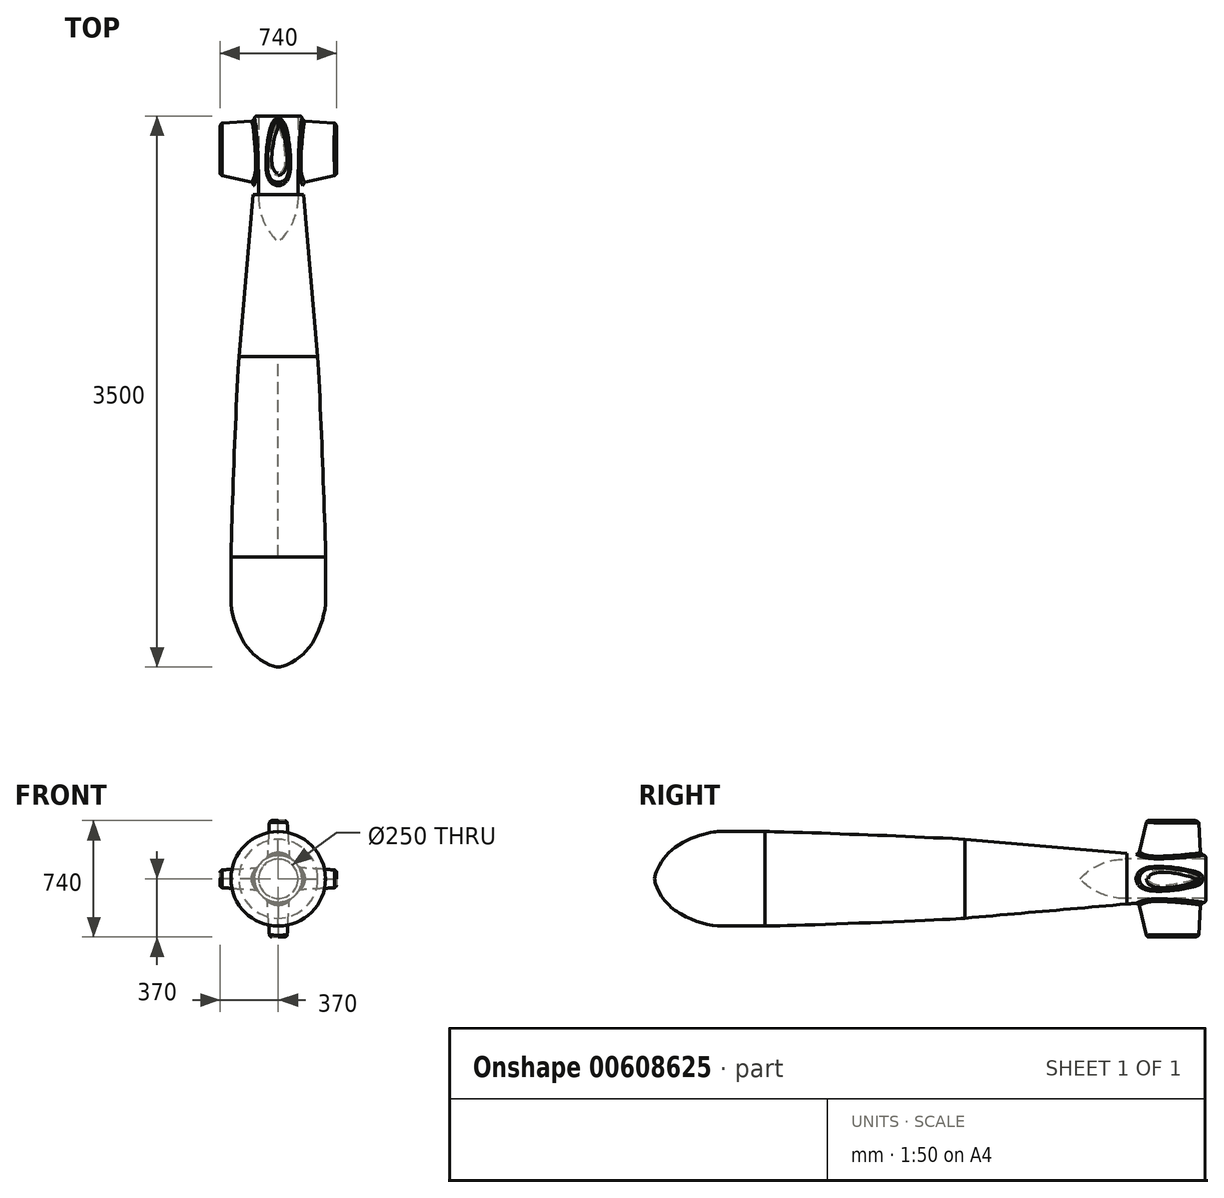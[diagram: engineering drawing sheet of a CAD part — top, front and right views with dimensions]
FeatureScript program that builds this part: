
annotation { "Feature Type Name" : "Feature", "Feature Type Description" : "" }
export const myFeature = defineFeature(function(context is Context, id is Id, definition is map)
    precondition{}
    {
        {
            var Q0;
            Q0=qCreatedBy(makeId("Right.planeOp"),FACE);
            var sketch = newSketch(context, id + "F0", { "sketchPlane" : qUnion([Q0])});
            skLineSegment(sketch, "E0", {"start": v(400, 300) * mm, "end": v(700, 300) * mm});
            skFitSpline(sketch, "E1", {"points": [v(0, 0) * mm, v(130, 200) * mm, v(400, 300) * mm], "startDerivative": vector(31.48, 314.8) * mm, "endDerivative": vector(229.22, 0) * mm});
            skFitSpline(sketch, "E2", {"points": [v(700, 300) * mm, v(1971.3, 250) * mm], "startDerivative": vector(450, 0) * mm, "endDerivative": vector(448.29, -39.22) * mm});
            skLineSegment(sketch, "E3", {"start": v(1971.3, 250) * mm, "end": v(3000, 160) * mm});
            skFitSpline(sketch, "E4", {"points": [v(3000, 160) * mm, v(3160, 150) * mm], "startDerivative": vector(150, -13.12) * mm, "endDerivative": vector(150, 0) * mm});
            skLineSegment(sketch, "E5", {"start": v(3160, 150) * mm, "end": v(3488, 150) * mm});
            skLineSegment(sketch, "E6", {"start": v(3500, 138) * mm, "end": v(3500, 137) * mm});
            skLineSegment(sketch, "E7", {"start": v(3488, 125) * mm, "end": v(2988, 125) * mm});
            skPoint(sketch, "E8.visualSharp", {"position": v(3500, 150) * mm});
            skArc(sketch, "E8.filletArc", {"start": v(3500, 138) * mm, "mid": v(3496.49, 146.49) * mm, "end": v(3488, 150) * mm});
            skPoint(sketch, "E9.visualSharp", {"position": v(3500, 125) * mm});
            skArc(sketch, "E9.filletArc", {"start": v(3488, 125) * mm, "mid": v(3496.49, 128.51) * mm, "end": v(3500, 137) * mm});
            skLineSegment(sketch, "E10", {"start": v(0, 0) * mm, "end": v(2700, 0) * mm});
            skArc(sketch, "E11", {"start": v(2988, 125) * mm, "mid": v(2831.02, 92.4) * mm, "end": v(2700, 0) * mm});
            skSolve(sketch);
        }
        {
            var Q0;
            Q0 = qSketchRegion(id + "F0", true);
            var Q1;
            Q1=sQuery(id+"F0.wireOp",EDGE,"E10");
            revolve(context, id + "F1", {"entities" : qUnion([Q0]), "axis" : qUnion([Q1]), "revolveType" : RevolveType.FULL});
        }
        {
            var Q0;
            Q0=qCreatedBy(makeId("Top.planeOp"),FACE);
            cPlane(context, id + "F2", {"entities" : qUnion([Q0]), "cplaneType" : CPlaneType.OFFSET, "offset" : 130 * mm, "width" : 150 * mm, "height" : 150 * mm});
        }
        {
            var Q0;
            Q0=qCreatedBy(id+"F2.planeOp",FACE);
            var sketch = newSketch(context, id + "F3", { "sketchPlane" : qUnion([Q0])});
            skLineSegment(sketch, "E12", {"start": v(0, 3070) * mm, "end": v(0, 3470) * mm, "construction": true});
            skLineSegment(sketch, "E13", {"start": v(0, 3120) * mm, "end": v(-60, 3120) * mm, "construction": true});
            skLineSegment(sketch, "E14", {"start": v(0, 3420) * mm, "end": v(-40, 3420) * mm, "construction": true});
            skLineSegment(sketch, "E15", {"start": v(-20, 3460) * mm, "end": v(0, 3460) * mm, "construction": true});
            skFitSpline(sketch, "E16", {"points": [v(0, 3070) * mm, v(-60, 3120) * mm, v(-40, 3420) * mm, v(-20, 3460) * mm, v(0, 3470) * mm], "startDerivative": vector(-255.23, 0) * mm, "endDerivative": vector(190.8, 35.78) * mm});
            skFitSpline(sketch, "E17.MirrorCS", {"points": [v(0, 3070) * mm, v(60, 3120) * mm, v(40, 3420) * mm, v(20, 3460) * mm, v(0, 3470) * mm], "startDerivative": vector(255.23, 0) * mm, "endDerivative": vector(-190.8, 35.78) * mm});
            skSolve(sketch);
        }
        {
            var Q0;
            Q0=qCreatedBy(makeId("Top.planeOp"),FACE);
            cPlane(context, id + "F4", {"entities" : qUnion([Q0]), "cplaneType" : CPlaneType.OFFSET, "offset" : 370 * mm, "width" : 150 * mm, "height" : 150 * mm});
        }
        {
            var Q0;
            Q0=qCreatedBy(id+"F4.planeOp",FACE);
            var sketch = newSketch(context, id + "F5", { "sketchPlane" : qUnion([Q0])});
            skLineSegment(sketch, "E18", {"start": v(0, 3125) * mm, "end": v(0, 3455) * mm, "construction": true});
            skLineSegment(sketch, "E19", {"start": v(0, 3175) * mm, "end": v(-50, 3175) * mm, "construction": true});
            skLineSegment(sketch, "E20", {"start": v(-27.5, 3400) * mm, "end": v(0, 3400) * mm, "construction": true});
            skFitSpline(sketch, "E21", {"points": [v(0, 3125) * mm, v(-50, 3175) * mm, v(-27.5, 3400) * mm, v(0, 3455) * mm], "startDerivative": vector(-223.25, 0) * mm, "endDerivative": vector(119.7, 143.64) * mm});
            skLineSegment(sketch, "E22", {"start": v(0, 3425) * mm, "end": v(-18.26, 3425) * mm, "construction": true});
            skFitSpline(sketch, "E23.MirrorCS", {"points": [v(0, 3125) * mm, v(50, 3175) * mm, v(27.5, 3400) * mm, v(0, 3455) * mm], "startDerivative": vector(223.25, 0) * mm, "endDerivative": vector(-119.7, 143.64) * mm});
            skSolve(sketch);
        }
        {
            var Q0;
            Q0 = qSketchRegion(id + "F3", true);
            var Q1;
            Q1 = qSketchRegion(id + "F5", true);
            loft(context, id + "F6", {"sheetProfilesArray" : [{ "sheetProfileEntities" : qUnion([Q0]) }, { "sheetProfileEntities" : qUnion([Q1]) }]});
        }
        {
            var Q0;
            Q0=makeQuery(id+"F6.opLoft","SWEPT_BODY",BODY,{"disambiguationData":[OSD([makeQuery(id+"F3.imprint","IMPRINT",FACE,{"disambiguationData":[TD([[makeQuery(id+"F3.imprint","IMPRINT",EDGE,{"derivedFrom":sQuery(id+"F3.wireOp",EDGE,"E16")}),-1.0]])]}),makeQuery(id+"F5.imprint","IMPRINT",FACE,{"disambiguationData":[TD([[makeQuery(id+"F5.imprint","IMPRINT",EDGE,{"derivedFrom":sQuery(id+"F5.wireOp",EDGE,"E21")}),-1.0]])]})])]});
            var Q1;
            Q1=sQuery(id+"F0.wireOp",EDGE,"E10");
            circularPattern(context, id + "F7", {"entities" : qUnion([Q0]), "axis" : qUnion([Q1]), "angle" : 360 * degree, "instanceCount" : 4, "equalSpace" : true});
        }
        {
            var Q0;
            Q0=makeQuery(id+"F1.opRevolve","SWEPT_BODY",BODY,{"disambiguationData":[OSD([sQuery(id+"F0.wireOp",EDGE,"E0"),sQuery(id+"F0.wireOp",EDGE,"E1"),sQuery(id+"F0.wireOp",EDGE,"E2"),sQuery(id+"F0.wireOp",EDGE,"E3"),sQuery(id+"F0.wireOp",EDGE,"E4"),sQuery(id+"F0.wireOp",EDGE,"E5"),sQuery(id+"F0.wireOp",EDGE,"E6"),sQuery(id+"F0.wireOp",EDGE,"E7"),sQuery(id+"F0.wireOp",EDGE,"E8.filletArc"),sQuery(id+"F0.wireOp",EDGE,"E9.filletArc"),sQuery(id+"F0.wireOp",EDGE,"E10"),sQuery(id+"F0.wireOp",EDGE,"E11")])]});
            var Q1;
            Q1=makeQuery(id+"F6.opLoft","SWEPT_BODY",BODY,{"disambiguationData":[OSD([makeQuery(id+"F3.imprint","IMPRINT",FACE,{"disambiguationData":[TD([[makeQuery(id+"F3.imprint","IMPRINT",EDGE,{"derivedFrom":sQuery(id+"F3.wireOp",EDGE,"E16")}),-1.0]])]}),makeQuery(id+"F5.imprint","IMPRINT",FACE,{"disambiguationData":[TD([[makeQuery(id+"F5.imprint","IMPRINT",EDGE,{"derivedFrom":sQuery(id+"F5.wireOp",EDGE,"E21")}),-1.0]])]})])]});
            var Q2;
            Q2=makeQuery(id+"F7.opPattern","COPY",BODY,{"derivedFrom":makeQuery(id+"F6.opLoft","SWEPT_BODY",BODY,{"disambiguationData":[OSD([makeQuery(id+"F3.imprint","IMPRINT",FACE,{"disambiguationData":[TD([[makeQuery(id+"F3.imprint","IMPRINT",EDGE,{"derivedFrom":sQuery(id+"F3.wireOp",EDGE,"E16")}),-1.0]])]}),makeQuery(id+"F5.imprint","IMPRINT",FACE,{"disambiguationData":[TD([[makeQuery(id+"F5.imprint","IMPRINT",EDGE,{"derivedFrom":sQuery(id+"F5.wireOp",EDGE,"E21")}),-1.0]])]})])]}),"instanceName":"1"});
            var Q3;
            Q3=makeQuery(id+"F7.opPattern","COPY",BODY,{"derivedFrom":makeQuery(id+"F6.opLoft","SWEPT_BODY",BODY,{"disambiguationData":[OSD([makeQuery(id+"F3.imprint","IMPRINT",FACE,{"disambiguationData":[TD([[makeQuery(id+"F3.imprint","IMPRINT",EDGE,{"derivedFrom":sQuery(id+"F3.wireOp",EDGE,"E16")}),-1.0]])]}),makeQuery(id+"F5.imprint","IMPRINT",FACE,{"disambiguationData":[TD([[makeQuery(id+"F5.imprint","IMPRINT",EDGE,{"derivedFrom":sQuery(id+"F5.wireOp",EDGE,"E21")}),-1.0]])]})])]}),"instanceName":"2"});
            var Q4;
            Q4=makeQuery(id+"F7.opPattern","COPY",BODY,{"derivedFrom":makeQuery(id+"F6.opLoft","SWEPT_BODY",BODY,{"disambiguationData":[OSD([makeQuery(id+"F3.imprint","IMPRINT",FACE,{"disambiguationData":[TD([[makeQuery(id+"F3.imprint","IMPRINT",EDGE,{"derivedFrom":sQuery(id+"F3.wireOp",EDGE,"E16")}),-1.0]])]}),makeQuery(id+"F5.imprint","IMPRINT",FACE,{"disambiguationData":[TD([[makeQuery(id+"F5.imprint","IMPRINT",EDGE,{"derivedFrom":sQuery(id+"F5.wireOp",EDGE,"E21")}),-1.0]])]})])]}),"instanceName":"3"});
            booleanBodies(context, id + "F8", {"operationType" : BooleanOperationType.UNION, "tools" : qUnion([Q0, Q1, Q2, Q3, Q4])});
        }
        {
            var Q0;
            {var subQ0=sQuery(id+"F5.wireOp",EDGE,"E23.MirrorCS");var subQ1=sQuery(id+"F5.wireOp",EDGE,"E21");var subQ2=sQuery(id+"F3.wireOp",EDGE,"E17.MirrorCS");var subQ3=sQuery(id+"F3.wireOp",EDGE,"E16");Q0=makeQuery(id+"F8.opBoolean","INTERSECT",EDGE,{"derivedFrom":[makeQuery(id+"F1.opRevolve","SWEPT_FACE",FACE,{"disambiguationData":[OSD([sQuery(id+"F0.wireOp",EDGE,"E5")])]}),makeQuery(id+"F6.opLoft","SWEPT_FACE",FACE,{"disambiguationData":[OSD([subQ3,subQ2,subQ1,subQ0]),TDD([makeQuery(id+"F3.imprint","INTERSECT",VERTEX,{"disambiguationData":[OD(0.0)],"derivedFrom":[subQ3,subQ2]}),makeQuery(id+"F3.imprint","INTERSECT",VERTEX,{"disambiguationData":[OD(1.0)],"derivedFrom":[subQ3,subQ2]}),makeQuery(id+"F3.imprint","IMPRINT",EDGE,{"derivedFrom":subQ2}),makeQuery(id+"F5.imprint","INTERSECT",VERTEX,{"disambiguationData":[OD(0.0)],"derivedFrom":[subQ1,subQ0]}),makeQuery(id+"F5.imprint","INTERSECT",VERTEX,{"disambiguationData":[OD(1.0)],"derivedFrom":[subQ1,subQ0]}),makeQuery(id+"F5.imprint","IMPRINT",EDGE,{"derivedFrom":subQ0})])]})]});}
            var Q1;
            {var subQ0=sQuery(id+"F5.wireOp",EDGE,"E21");var subQ1=sQuery(id+"F5.wireOp",EDGE,"E23.MirrorCS");var subQ2=sQuery(id+"F3.wireOp",EDGE,"E16");var subQ3=sQuery(id+"F3.wireOp",EDGE,"E17.MirrorCS");Q1=makeQuery(id+"F8.opBoolean","INTERSECT",EDGE,{"derivedFrom":[makeQuery(id+"F1.opRevolve","SWEPT_FACE",FACE,{"disambiguationData":[OSD([sQuery(id+"F0.wireOp",EDGE,"E5")])]}),makeQuery(id+"F7.opPattern","COPY",FACE,{"derivedFrom":makeQuery(id+"F6.opLoft","SWEPT_FACE",FACE,{"disambiguationData":[OSD([subQ2,subQ3,subQ0,subQ1]),TDD([makeQuery(id+"F3.imprint","INTERSECT",VERTEX,{"disambiguationData":[OD(0.0)],"derivedFrom":[subQ2,subQ3]}),makeQuery(id+"F3.imprint","INTERSECT",VERTEX,{"disambiguationData":[OD(1.0)],"derivedFrom":[subQ2,subQ3]}),makeQuery(id+"F3.imprint","IMPRINT",EDGE,{"derivedFrom":subQ2}),makeQuery(id+"F5.imprint","INTERSECT",VERTEX,{"disambiguationData":[OD(0.0)],"derivedFrom":[subQ0,subQ1]}),makeQuery(id+"F5.imprint","INTERSECT",VERTEX,{"disambiguationData":[OD(1.0)],"derivedFrom":[subQ0,subQ1]}),makeQuery(id+"F5.imprint","IMPRINT",EDGE,{"derivedFrom":subQ0})])]}),"instanceName":"1"})]});}
            var Q2;
            {var subQ0=sQuery(id+"F5.wireOp",EDGE,"E21");var subQ1=sQuery(id+"F5.wireOp",EDGE,"E23.MirrorCS");var subQ2=sQuery(id+"F3.wireOp",EDGE,"E16");var subQ3=sQuery(id+"F3.wireOp",EDGE,"E17.MirrorCS");Q2=makeQuery(id+"F8.opBoolean","INTERSECT",EDGE,{"derivedFrom":[makeQuery(id+"F1.opRevolve","SWEPT_FACE",FACE,{"disambiguationData":[OSD([sQuery(id+"F0.wireOp",EDGE,"E5")])]}),makeQuery(id+"F7.opPattern","COPY",FACE,{"derivedFrom":makeQuery(id+"F6.opLoft","SWEPT_FACE",FACE,{"disambiguationData":[OSD([subQ2,subQ3,subQ0,subQ1]),TDD([makeQuery(id+"F3.imprint","INTERSECT",VERTEX,{"disambiguationData":[OD(0.0)],"derivedFrom":[subQ2,subQ3]}),makeQuery(id+"F3.imprint","INTERSECT",VERTEX,{"disambiguationData":[OD(1.0)],"derivedFrom":[subQ2,subQ3]}),makeQuery(id+"F3.imprint","IMPRINT",EDGE,{"derivedFrom":subQ2}),makeQuery(id+"F5.imprint","INTERSECT",VERTEX,{"disambiguationData":[OD(0.0)],"derivedFrom":[subQ0,subQ1]}),makeQuery(id+"F5.imprint","INTERSECT",VERTEX,{"disambiguationData":[OD(1.0)],"derivedFrom":[subQ0,subQ1]}),makeQuery(id+"F5.imprint","IMPRINT",EDGE,{"derivedFrom":subQ0})])]}),"instanceName":"2"})]});}
            var Q3;
            {var subQ0=sQuery(id+"F5.wireOp",EDGE,"E21");var subQ1=sQuery(id+"F5.wireOp",EDGE,"E23.MirrorCS");var subQ2=sQuery(id+"F3.wireOp",EDGE,"E16");var subQ3=sQuery(id+"F3.wireOp",EDGE,"E17.MirrorCS");Q3=makeQuery(id+"F8.opBoolean","INTERSECT",EDGE,{"derivedFrom":[makeQuery(id+"F1.opRevolve","SWEPT_FACE",FACE,{"disambiguationData":[OSD([sQuery(id+"F0.wireOp",EDGE,"E5")])]}),makeQuery(id+"F7.opPattern","COPY",FACE,{"derivedFrom":makeQuery(id+"F6.opLoft","SWEPT_FACE",FACE,{"disambiguationData":[OSD([subQ2,subQ3,subQ0,subQ1]),TDD([makeQuery(id+"F3.imprint","INTERSECT",VERTEX,{"disambiguationData":[OD(0.0)],"derivedFrom":[subQ2,subQ3]}),makeQuery(id+"F3.imprint","INTERSECT",VERTEX,{"disambiguationData":[OD(1.0)],"derivedFrom":[subQ2,subQ3]}),makeQuery(id+"F3.imprint","IMPRINT",EDGE,{"derivedFrom":subQ2}),makeQuery(id+"F5.imprint","INTERSECT",VERTEX,{"disambiguationData":[OD(0.0)],"derivedFrom":[subQ0,subQ1]}),makeQuery(id+"F5.imprint","INTERSECT",VERTEX,{"disambiguationData":[OD(1.0)],"derivedFrom":[subQ0,subQ1]}),makeQuery(id+"F5.imprint","IMPRINT",EDGE,{"derivedFrom":subQ0})])]}),"instanceName":"3"})]});}
            fillet(context, id + "F9", {"entities" : qUnion([Q0, Q1, Q2, Q3]), "radius" : 20 * mm, "tangentPropagation" : true, "rho" : 0.1, "crossSection" : FilletCrossSection.CONIC, "allowEdgeOverflow" : false});
        }
        {
            var Q0;
            {var subQ0=sQuery(id+"F5.wireOp",EDGE,"E23.MirrorCS");var subQ1=sQuery(id+"F5.wireOp",EDGE,"E21");Q0=makeQuery(id+"F6.opLoft","MID_CAP_EDGE",EDGE,{"disambiguationData":[OSD([subQ1,subQ0]),TDD([makeQuery(id+"F5.imprint","INTERSECT",VERTEX,{"disambiguationData":[OD(0.0)],"derivedFrom":[subQ1,subQ0]}),makeQuery(id+"F5.imprint","INTERSECT",VERTEX,{"disambiguationData":[OD(1.0)],"derivedFrom":[subQ1,subQ0]}),makeQuery(id+"F5.imprint","IMPRINT",EDGE,{"derivedFrom":subQ0})])],"capPos":1.0});}
            var Q1;
            {var subQ0=sQuery(id+"F5.wireOp",EDGE,"E23.MirrorCS");var subQ1=sQuery(id+"F5.wireOp",EDGE,"E21");Q1=makeQuery(id+"F7.opPattern","COPY",EDGE,{"derivedFrom":makeQuery(id+"F6.opLoft","MID_CAP_EDGE",EDGE,{"disambiguationData":[OSD([subQ1,subQ0]),TDD([makeQuery(id+"F5.imprint","INTERSECT",VERTEX,{"disambiguationData":[OD(0.0)],"derivedFrom":[subQ1,subQ0]}),makeQuery(id+"F5.imprint","INTERSECT",VERTEX,{"disambiguationData":[OD(1.0)],"derivedFrom":[subQ1,subQ0]}),makeQuery(id+"F5.imprint","IMPRINT",EDGE,{"derivedFrom":subQ0})])],"capPos":1.0}),"instanceName":"1"});}
            var Q2;
            {var subQ0=sQuery(id+"F5.wireOp",EDGE,"E21");var subQ1=sQuery(id+"F5.wireOp",EDGE,"E23.MirrorCS");Q2=makeQuery(id+"F7.opPattern","COPY",EDGE,{"derivedFrom":makeQuery(id+"F6.opLoft","MID_CAP_EDGE",EDGE,{"disambiguationData":[OSD([subQ0,subQ1]),TDD([makeQuery(id+"F5.imprint","INTERSECT",VERTEX,{"disambiguationData":[OD(0.0)],"derivedFrom":[subQ0,subQ1]}),makeQuery(id+"F5.imprint","INTERSECT",VERTEX,{"disambiguationData":[OD(1.0)],"derivedFrom":[subQ0,subQ1]}),makeQuery(id+"F5.imprint","IMPRINT",EDGE,{"derivedFrom":subQ0})])],"capPos":1.0}),"instanceName":"2"});}
            var Q3;
            {var subQ0=sQuery(id+"F5.wireOp",EDGE,"E21");var subQ1=sQuery(id+"F5.wireOp",EDGE,"E23.MirrorCS");Q3=makeQuery(id+"F7.opPattern","COPY",EDGE,{"derivedFrom":makeQuery(id+"F6.opLoft","MID_CAP_EDGE",EDGE,{"disambiguationData":[OSD([subQ0,subQ1]),TDD([makeQuery(id+"F5.imprint","INTERSECT",VERTEX,{"disambiguationData":[OD(0.0)],"derivedFrom":[subQ0,subQ1]}),makeQuery(id+"F5.imprint","INTERSECT",VERTEX,{"disambiguationData":[OD(1.0)],"derivedFrom":[subQ0,subQ1]}),makeQuery(id+"F5.imprint","IMPRINT",EDGE,{"derivedFrom":subQ0})])],"capPos":1.0}),"instanceName":"3"});}
            fillet(context, id + "F10", {"entities" : qUnion([Q0, Q1, Q2, Q3]), "radius" : 15 * mm, "tangentPropagation" : true, "rho" : 0.3, "crossSection" : FilletCrossSection.CONIC, "allowEdgeOverflow" : false});
        }
    });
